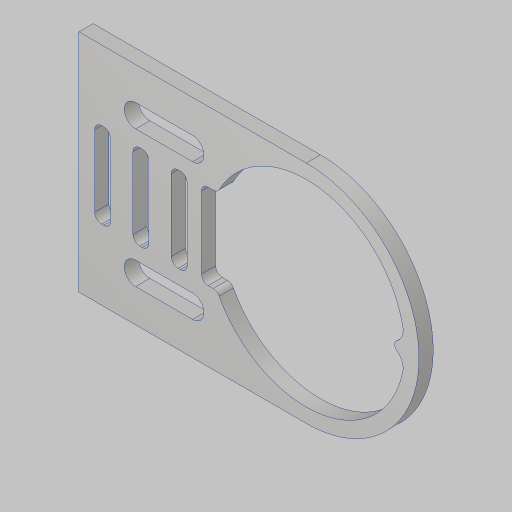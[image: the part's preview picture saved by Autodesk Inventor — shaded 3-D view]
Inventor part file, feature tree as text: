
AUTODESK INVENTOR PART (.ipt)
format: ipt  version: 2023.5 (Build 275446000, 446)  size: 356,864 bytes
history: native  units: in
note: dims shown in document units (in); Inventor stores cm internally (conversion verified against a paired STEP export)
features: extrude x4, sketch x4, fillet x2, projected_geometry x1
ambient origin geometry x8: Origin, YZ Plane, XZ Plane, XY Plane, X Axis, Y Axis, Z Axis, Center Point
bodies: Solid1 (feature_tree)
feature tree (11):
  extrude  "Extrusion1"  Depth=1.983in
  extrude  "Extrusion2"  Depth=0.125in
  extrude  "Extrusion3"  Depth=0.75in
  fillet  "Fillet1"  Radius=0.4901in
  extrude  "Extrusion4"  Depth=0.6151in
  fillet  "Fillet2"  Radius=0.125in
  sketch  "Sketch1"  dims[d0=2.0in d1=1.983in]
  sketch  "Sketch2"  dims[d3=0.125in d4=0.0in d6=0.125in]
  sketch  "Sketch3"  dims[d7=0.25in d8=0.75in d9=0.4901in]
  projected_geometry  "Projected Loop1"
  sketch  "Sketch4"  dims[d10=1.078in d11=0.6151in d12=0.125in d13=0.0in d14=0.0938in d15=0.825in d16=0.125in d17=0.0in d18=0.13in d19=0.125in d20=0.1969in d21=0.1969in d22=0.14in d23=0.14in d24=0.14in d25=0.75in d26=0.75in d27=0.75in d28=0.1393in d29=0.201in d30=0.201in d33=0.5in d34=0.5in d35=0.125in d36=0.125in d37=0.75in d38=1.0in d39=0.0in d40=0.06in]
